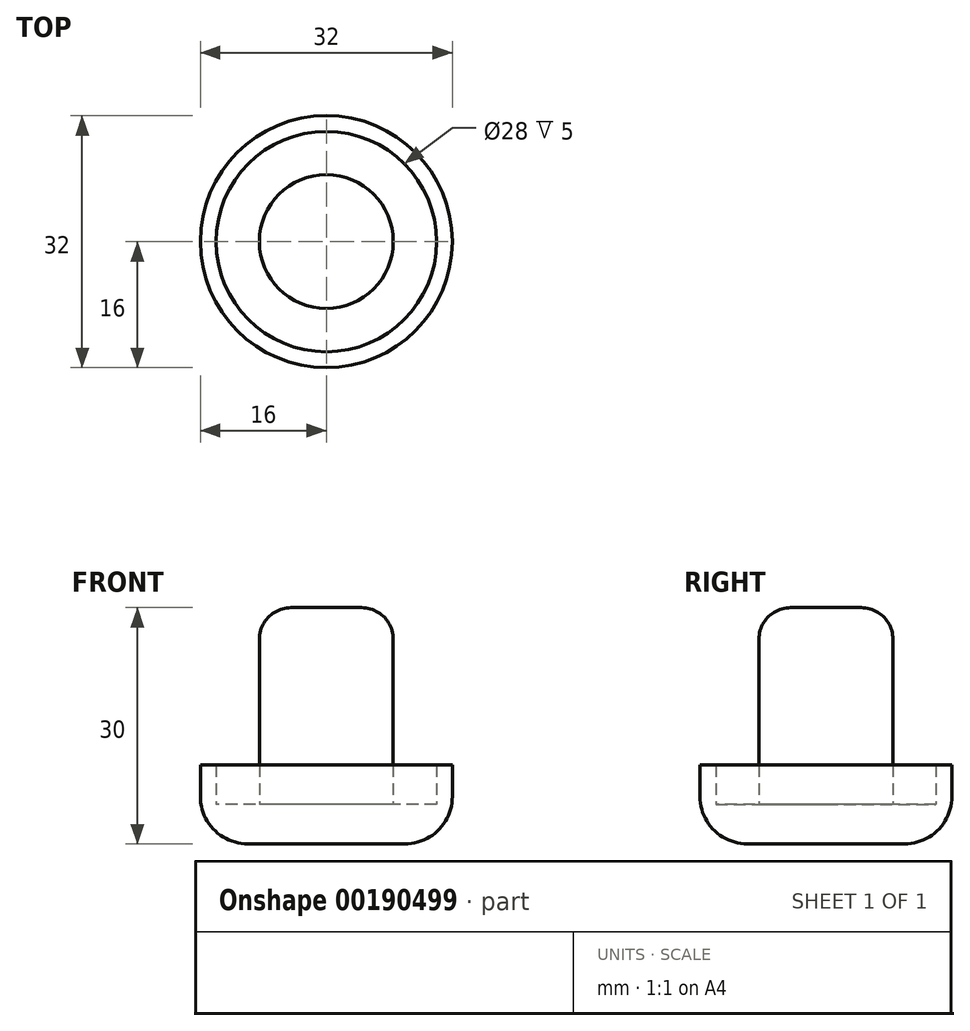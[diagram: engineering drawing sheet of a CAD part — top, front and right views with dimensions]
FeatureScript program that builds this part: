
annotation { "Feature Type Name" : "Feature", "Feature Type Description" : "" }
export const myFeature = defineFeature(function(context is Context, id is Id, definition is map)
    precondition{}
    {
        {
            var Q0;
            Q0=qCreatedBy(makeId("Top.planeOp"),FACE);
            var sketch = newSketch(context, id + "F0", { "sketchPlane" : qUnion([Q0])});
            skCircle(sketch, "E0", {"center": v(0, 0) * mm, "radius": 8.5 * mm});
            skCircle(sketch, "E1", {"center": v(0, 0) * mm, "radius": 14 * mm});
            skCircle(sketch, "E2", {"center": v(0, 0) * mm, "radius": 16 * mm});
            skSolve(sketch);
        }
        {
            var Q0;
            Q0=makeQuery(id+"F0.imprint","IMPRINT",FACE,{"disambiguationData":[TD([[makeQuery(id+"F0.imprint","IMPRINT",EDGE,{"derivedFrom":sQuery(id+"F0.wireOp",EDGE,"E0")}),1.0]])]});
            extrude(context, id + "F1", {"entities" : qUnion([Q0]), "depth" : 30 * mm});
        }
        {
            var Q0;
            Q0=makeQuery(id+"F0.imprint","IMPRINT",FACE,{"disambiguationData":[TD([[makeQuery(id+"F0.imprint","IMPRINT",EDGE,{"derivedFrom":sQuery(id+"F0.wireOp",EDGE,"E0")}),-1.0]])]});
            extrude(context, id + "F2", {"entities" : qUnion([Q0]), "operationType" : NewBodyOperationType.ADD, "depth" : 5 * mm});
        }
        {
            var Q0;
            Q0=makeQuery(id+"F0.imprint","IMPRINT",FACE,{"disambiguationData":[TD([[makeQuery(id+"F0.imprint","IMPRINT",EDGE,{"derivedFrom":sQuery(id+"F0.wireOp",EDGE,"E1")}),-1.0]])]});
            extrude(context, id + "F3", {"entities" : qUnion([Q0]), "operationType" : NewBodyOperationType.ADD, "depth" : 10 * mm});
        }
        {
            var Q0;
            Q0=makeQuery(id+"F1.opExtrude","CAP_EDGE",EDGE,{"disambiguationData":[OSD([sQuery(id+"F0.wireOp",EDGE,"E0")])],"isStart":false});
            fillet(context, id + "F4", {"entities" : qUnion([Q0]), "radius" : 4 * mm, "tangentPropagation" : true, "allowEdgeOverflow" : false});
        }
        {
            var Q0;
            Q0=makeQuery(id+"F3.opExtrude","CAP_EDGE",EDGE,{"disambiguationData":[OSD([sQuery(id+"F0.wireOp",EDGE,"E2")])],"isStart":true});
            fillet(context, id + "F5", {"entities" : qUnion([Q0]), "radius" : 6 * mm, "allowEdgeOverflow" : false});
        }
    });
